# Revit family: JOMA_Balksko kombi_Grundform 238
name_source: partatom
category: Structural Connections
revit_build: Autodesk Revit Structure 2012 (Build: 20110309_2315(x64)
units: mm (PartAtom-declared; Revit-internal decimal feet)

## types (4) — shared parameters
D = 37 mm  [stored 0.121391 ft]
Default Elevation = 1219 mm
E = 37 mm  [stored 0.121391 ft]
F = 70 mm  [stored 0.229659 ft]
Grundform 238 = Yes
Länk Joma Dimensioneringsverktyg = http://www.joma.se
Material = Varmförzinkad stålplåt
Typ = GRUNDFORM 238
Vikt = 0,24
X = 35 mm
Y = 52 mm

## per-type parameters (varying)
| type | A | B |
| 5240099  40x99 | 40 mm  [stored 0.131234 ft] | 99 mm  [stored 0.324803 ft] |
| 5245096  45x96 | 45 mm  [stored 0.147638 ft] | 96 mm  [stored 0.314961 ft] |
| 5248095  48x95 | 48 mm  [stored 0.15748 ft] | 95 mm |
| 5251093  51x93 | 51 mm | 93 mm  [stored 0.305118 ft] |

note: [stored X ft] marks values corroborated as IEEE doubles in the binary element streams (Revit-internal decimal feet)

## geometry (parser evidence)
native form markers: Sweep x2
no freeform markers — native parametric forms only
